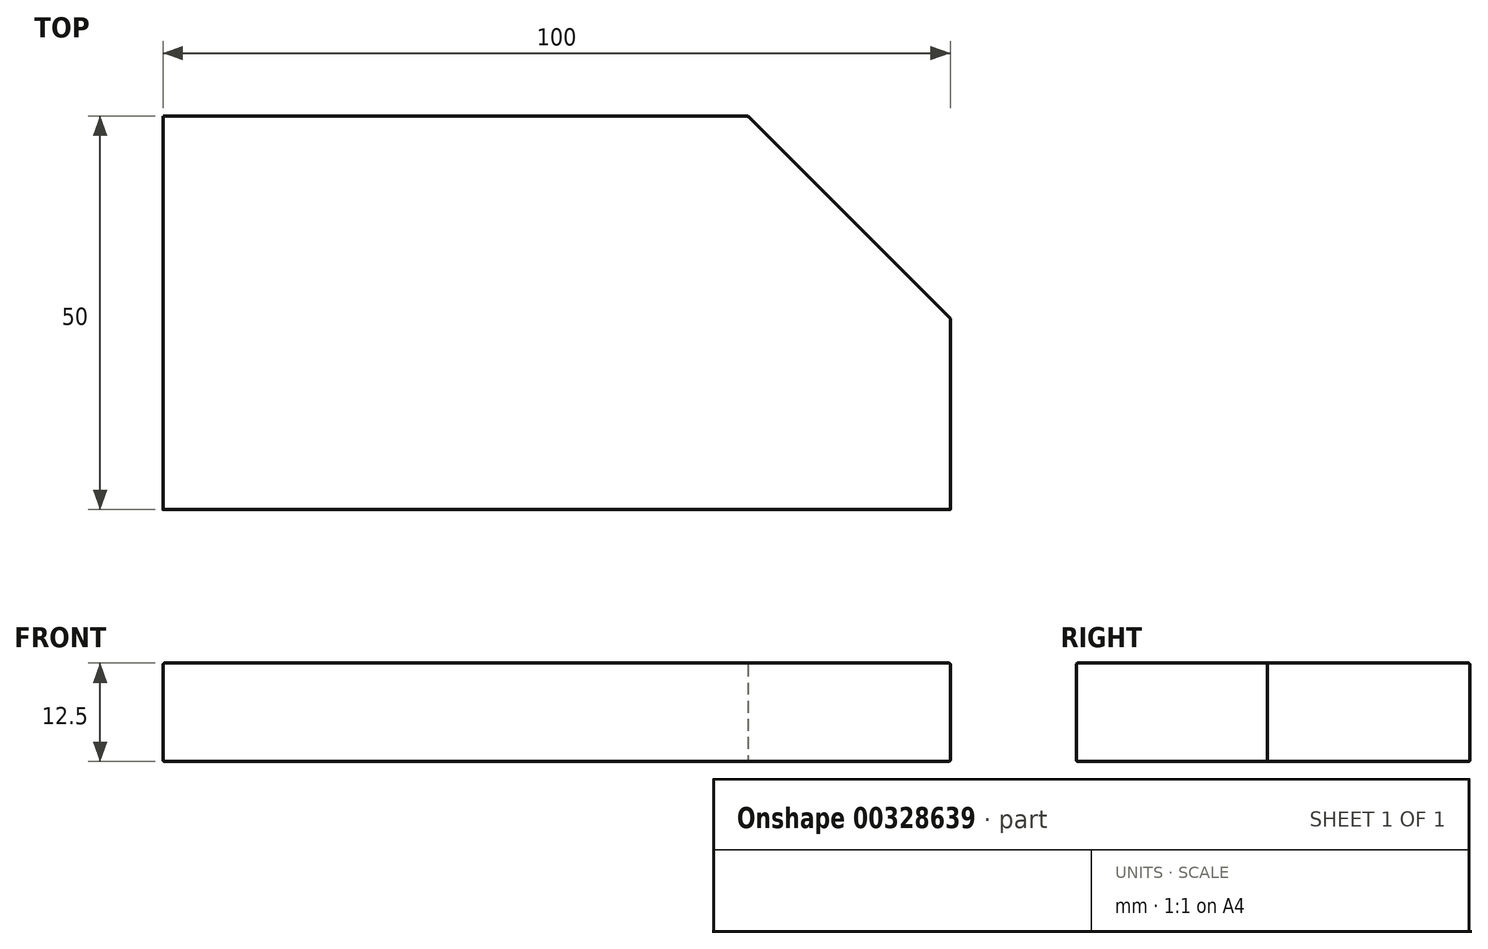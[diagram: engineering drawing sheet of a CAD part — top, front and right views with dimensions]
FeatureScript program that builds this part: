
annotation { "Feature Type Name" : "Feature", "Feature Type Description" : "" }
export const myFeature = defineFeature(function(context is Context, id is Id, definition is map)
    precondition{}
    {
        {
            var Q0;
            Q0=qCreatedBy(makeId("Top.planeOp"),FACE);
            var sketch = newSketch(context, id + "F0", { "sketchPlane" : qUnion([Q0])});
            skLineSegment(sketch, "E0.bottom", {"start": v(0, 0) * mm, "end": v(100, 0) * mm});
            skLineSegment(sketch, "E0.top", {"start": v(0, 50) * mm, "end": v(100, 50) * mm});
            skLineSegment(sketch, "E0.left", {"start": v(0, 0) * mm, "end": v(0, 50) * mm});
            skLineSegment(sketch, "E0.right", {"start": v(100, 0) * mm, "end": v(100, 50) * mm});
            skSolve(sketch);
        }
        {
            var Q0;
            Q0=qSketchRegion(id+"F0",true);
            extrude(context, id + "F1", {"entities" : qUnion([Q0]), "oppositeDirection" : true, "depth" : 12.5 * mm});
        }
        {
            var Q0;
            Q0=makeQuery(id+"F1.opExtrude","SWEPT_EDGE",EDGE,{"disambiguationData":[OSD([sQuery(id+"F0.wireOp",EDGE,"E0.top"),sQuery(id+"F0.wireOp",EDGE,"E0.right")])]});
            chamfer(context, id + "F2", {"entities" : qUnion([Q0]), "width" : 25.7 * mm, "tangentPropagation" : true});
        }
        {
            var Q0;
            Q0=makeQuery(id+"F1.opExtrude","CAP_FACE",FACE,{"disambiguationData":[OSD([sQuery(id+"F0.wireOp",EDGE,"E0.bottom"),sQuery(id+"F0.wireOp",EDGE,"E0.top"),sQuery(id+"F0.wireOp",EDGE,"E0.left"),sQuery(id+"F0.wireOp",EDGE,"E0.right")])],"isStart":true});
            var Q1;
            Q1=makeQuery(id+"F1.opExtrude","CAP_FACE",FACE,{"disambiguationData":[OSD([sQuery(id+"F0.wireOp",EDGE,"E0.bottom"),sQuery(id+"F0.wireOp",EDGE,"E0.top"),sQuery(id+"F0.wireOp",EDGE,"E0.left"),sQuery(id+"F0.wireOp",EDGE,"E0.right")])],"isStart":false});
            fillet(context, id + "F3", {"entities" : qUnion([Q0, Q1]), "radius" : .2 * mm, "tangentPropagation" : true, "allowEdgeOverflow" : false});
        }
    });
